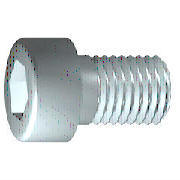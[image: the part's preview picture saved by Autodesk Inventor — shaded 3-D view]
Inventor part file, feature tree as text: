
AUTODESK INVENTOR PART (.ipt)
format: ipt  version: 2022 (Build 260153000, 153)  size: 196,608 bytes
history: native  units: mm (DEFAULTED — no unit token found)
features: sketch x2, other x1, extrude x1, plane x1, fillet x1
ambient origin geometry x7: Origin, YZ Plane, XY Plane, X Axis, Y Axis, Z Axis, Center Point
bodies: Solid1 (feature_tree)
feature tree (6):
  other  "Körper"
  extrude  "Loch"  Depth=3.0mm
  plane  "Work Plane1"
  fillet  "Fillet2"  Radius=3.0mm
  sketch  "Skizze1"  dims[d1=8.75mm d2=0.306825mm d3=3.0mm]
  sketch  "Skizze2"  dims[d4=1.3mm d5=60.0deg d6=3.0mm d7=3.0mm d8=2.886751mm d9=5.5mm d10=90.0deg d11=10.0mm d12=0.0mm d13=8.75mm d14=0.0mm d15=0.306725mm d16=0.306725mm d17=0.3mm d19=0.0mm d26=10.0mm d27=45.0deg d28=0.0mm d29=0.0mm d30=0.1mm]
